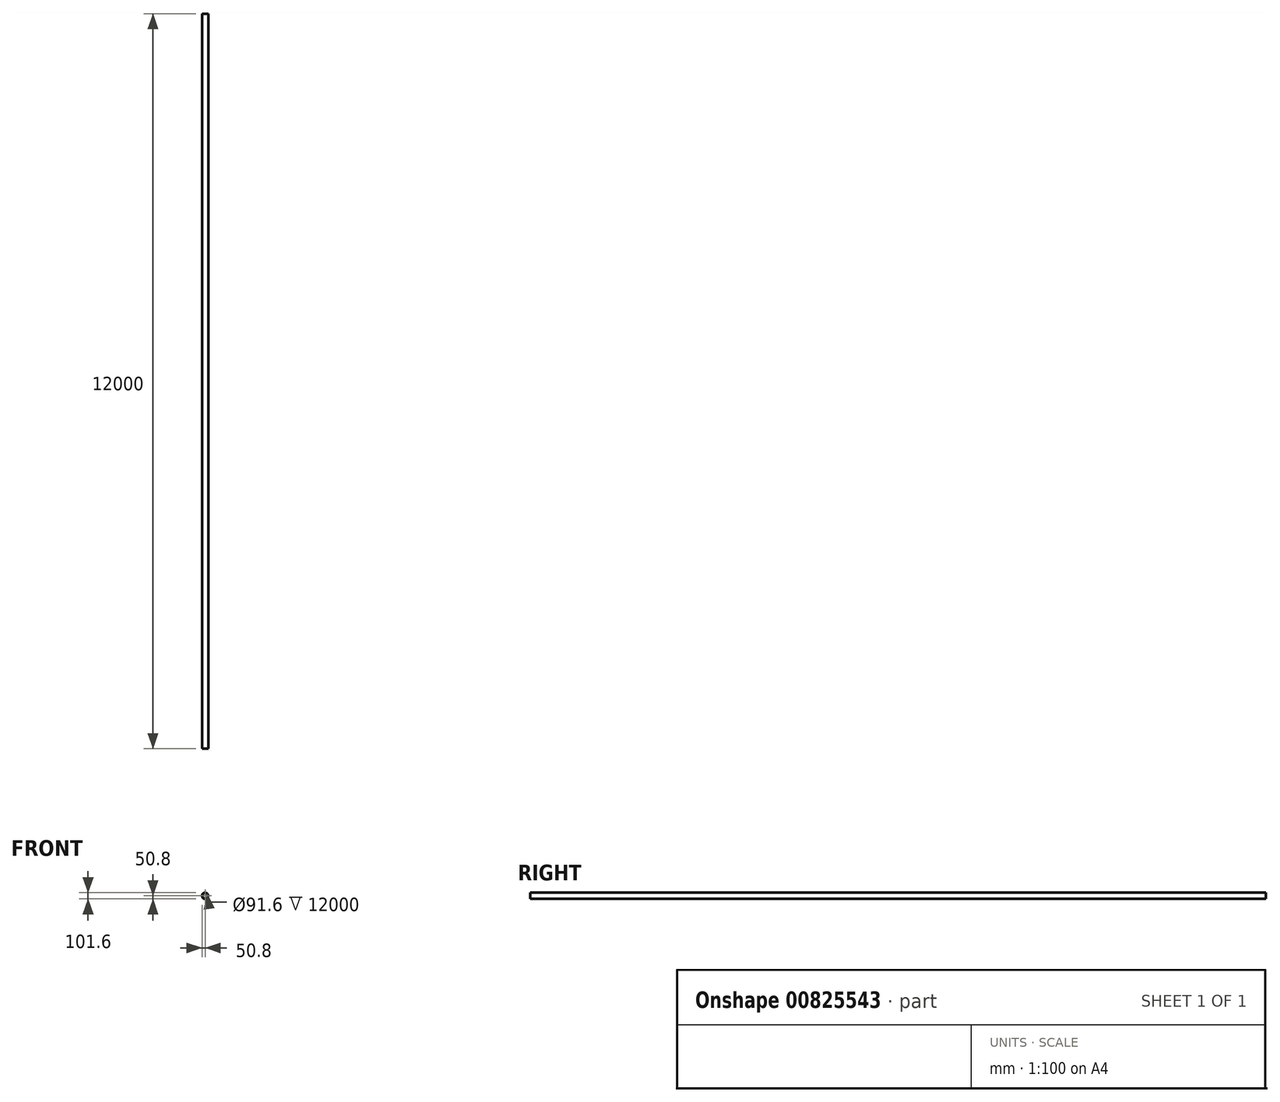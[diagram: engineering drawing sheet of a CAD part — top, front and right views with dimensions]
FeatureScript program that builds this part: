
annotation { "Feature Type Name" : "Feature", "Feature Type Description" : "" }
export const myFeature = defineFeature(function(context is Context, id is Id, definition is map)
    precondition{}
    {
        {
            var Q0;
            Q0=qCreatedBy(makeId("Front.planeOp"),FACE);
            var sketch = newSketch(context, id + "F0", { "sketchPlane" : qUnion([Q0])});
            skCircle(sketch, "E0", {"center": v(0, 0) * mm, "radius": 50.8 * mm});
            skCircle(sketch, "E1", {"center": v(0, 0) * mm, "radius": 45.8 * mm});
            skSolve(sketch);
        }
        {
            var Q0;
            Q0 = qSketchRegion(id + "F0", true);
            extrude(context, id + "F1", {"entities" : qUnion([Q0]), "depth" : 12000 * mm, "offsetDistance" : 25.4 * mm});
        }
    });
